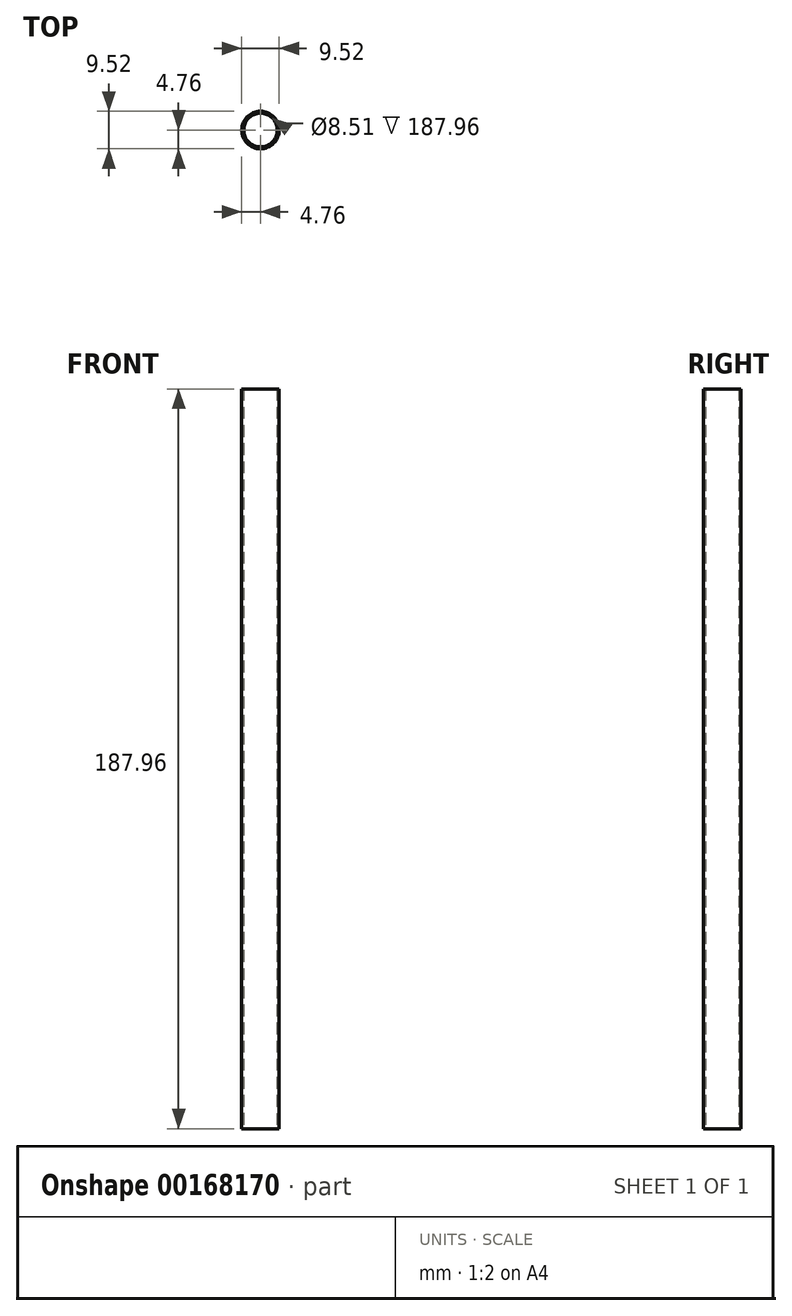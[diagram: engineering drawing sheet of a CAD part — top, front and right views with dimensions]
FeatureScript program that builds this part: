
annotation { "Feature Type Name" : "Feature", "Feature Type Description" : "" }
export const myFeature = defineFeature(function(context is Context, id is Id, definition is map)
    precondition{}
    {
        {
            var Q0;
            Q0=qCreatedBy(makeId("Top.planeOp"),FACE);
            var sketch = newSketch(context, id + "F0", { "sketchPlane" : qUnion([Q0])});
            skCircle(sketch, "E0", {"center": v(0, 0) * mm, "radius": 4.76 * mm});
            skCircle(sketch, "E1", {"center": v(0, 0) * mm, "radius": 4.25 * mm});
            skSolve(sketch);
        }
        {
            var Q0;
            Q0 = qSketchRegion(id + "F0", true);
            extrude(context, id + "F1", {"entities" : qUnion([Q0]), "depth" : 187.96 * mm});
        }
    });
